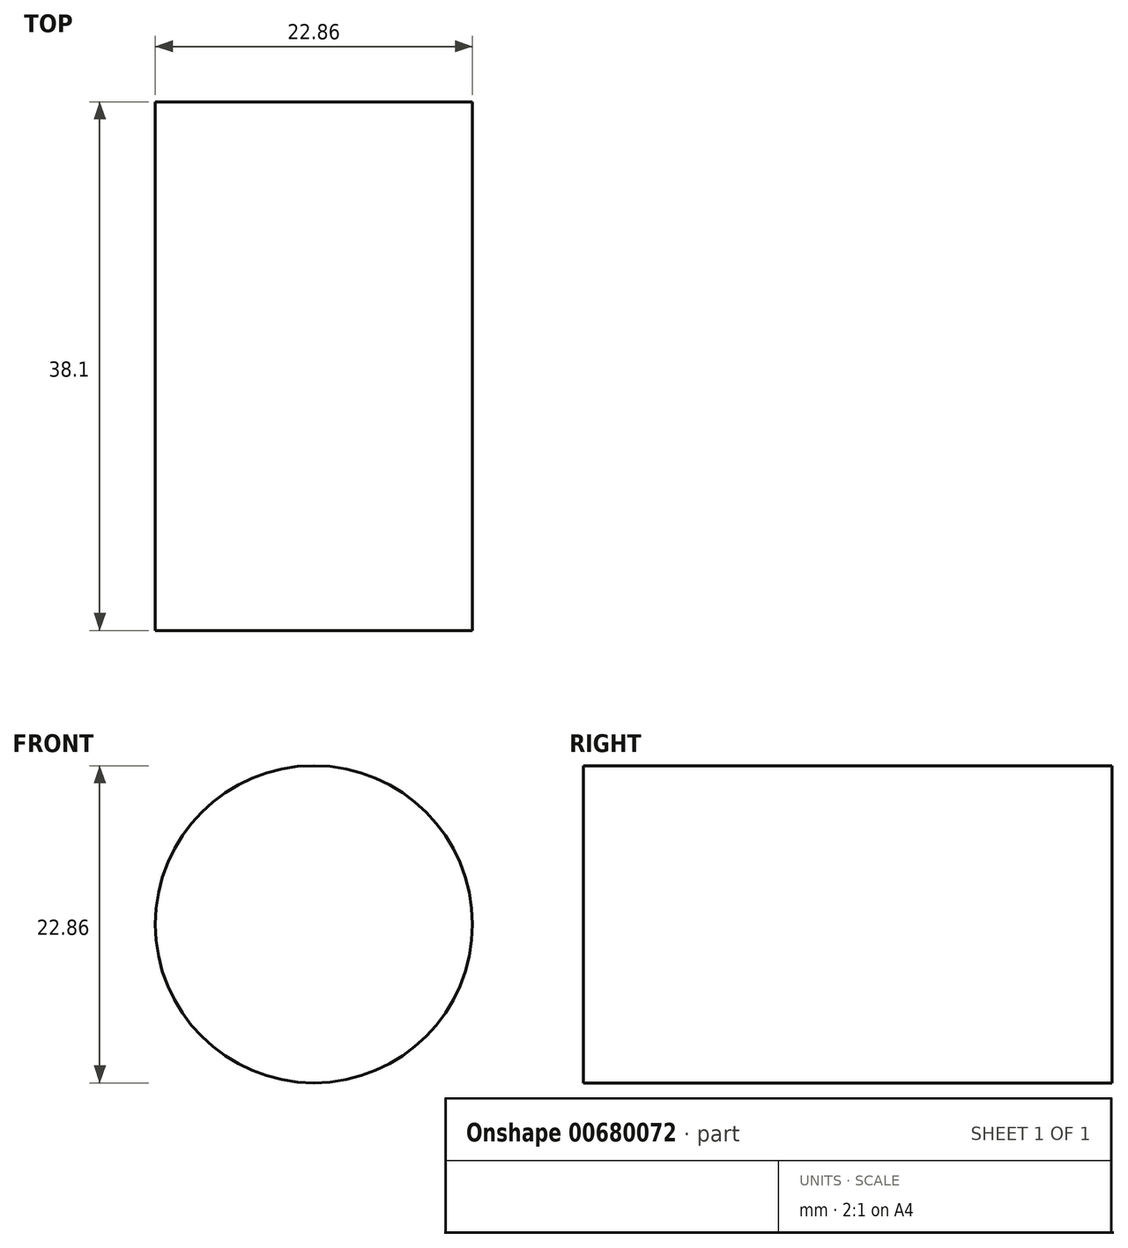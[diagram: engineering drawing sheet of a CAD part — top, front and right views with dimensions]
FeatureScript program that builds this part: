
annotation { "Feature Type Name" : "Feature", "Feature Type Description" : "" }
export const myFeature = defineFeature(function(context is Context, id is Id, definition is map)
    precondition{}
    {
        {
            var Q0;
            Q0=qCreatedBy(makeId("Front.planeOp"),FACE);
            var sketch = newSketch(context, id + "F0", { "sketchPlane" : qUnion([Q0])});
            skCircle(sketch, "E0", {"center": v(0, 0) * mm, "radius": 11.43 * mm});
            skSolve(sketch);
        }
        {
            var Q0;
            Q0=makeQuery(id+"F0.imprint","IMPRINT",FACE,{"disambiguationData":[TD([[makeQuery(id+"F0.imprint","IMPRINT",EDGE,{"derivedFrom":sQuery(id+"F0.wireOp",EDGE,"E0")}),1.0]])]});
            extrude(context, id + "F1", {"entities" : qUnion([Q0]), "depth" : 38.1 * mm, "offsetDistance" : 25.4 * mm});
        }
    });
